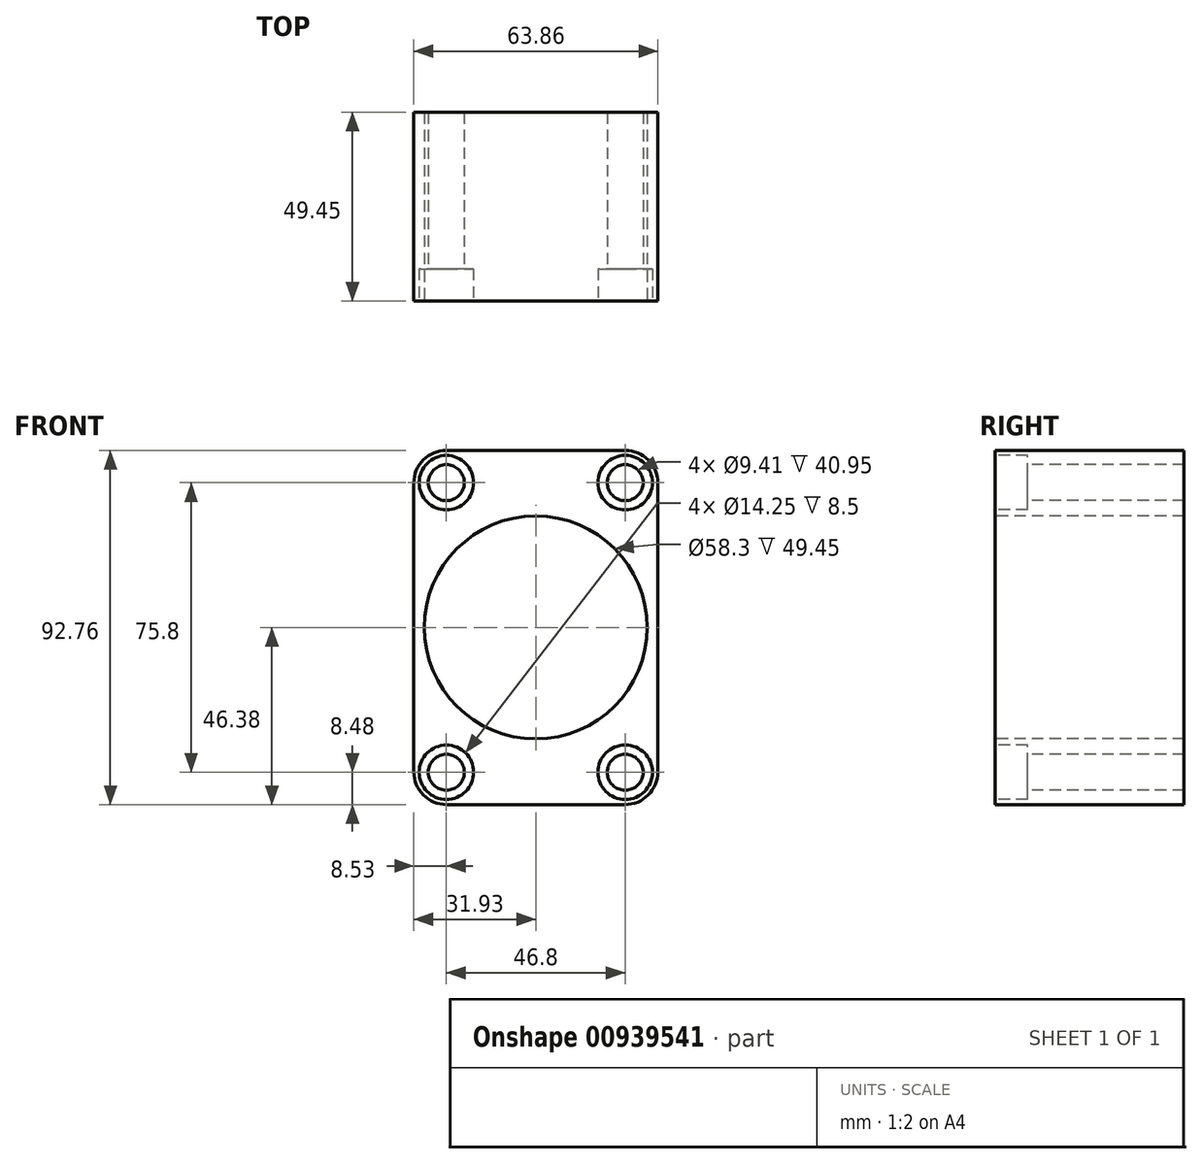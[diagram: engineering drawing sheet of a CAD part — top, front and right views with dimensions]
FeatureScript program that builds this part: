
annotation { "Feature Type Name" : "Feature", "Feature Type Description" : "" }
export const myFeature = defineFeature(function(context is Context, id is Id, definition is map)
    precondition{}
    {
        {
            var Q0;
            Q0=qCreatedBy(makeId("Front.planeOp"),FACE);
            var sketch = newSketch(context, id + "F0", { "sketchPlane" : qUnion([Q0])});
            skLineSegment(sketch, "E0.bottom", {"start": v(-31.93, -46.38) * mm, "end": v(31.93, -46.38) * mm});
            skLineSegment(sketch, "E0.top", {"start": v(-31.93, 46.38) * mm, "end": v(31.93, 46.38) * mm});
            skLineSegment(sketch, "E0.left", {"start": v(-31.93, -46.38) * mm, "end": v(-31.93, 46.38) * mm});
            skLineSegment(sketch, "E0.right", {"start": v(31.93, -46.38) * mm, "end": v(31.93, 46.38) * mm});
            skPoint(sketch, "E0.middle", {"position": v(0, 0) * mm});
            skSolve(sketch);
        }
        {
            var Q0;
            Q0 = qSketchRegion(id + "F0", true);
            extrude(context, id + "F1", {"entities" : qUnion([Q0]), "depth" : 49.45 * mm, "offsetDistance" : 25 * mm});
        }
        {
            var Q0;
            Q0=makeQuery(id+"F1.opExtrude","SWEPT_EDGE",EDGE,{"disambiguationData":[OSD([sQuery(id+"F0.wireOp",EDGE,"E0.top"),sQuery(id+"F0.wireOp",EDGE,"E0.right")])]});
            var Q1;
            Q1=makeQuery(id+"F1.opExtrude","SWEPT_EDGE",EDGE,{"disambiguationData":[OSD([sQuery(id+"F0.wireOp",EDGE,"E0.top"),sQuery(id+"F0.wireOp",EDGE,"E0.left")])]});
            var Q2;
            Q2=makeQuery(id+"F1.opExtrude","SWEPT_EDGE",EDGE,{"disambiguationData":[OSD([sQuery(id+"F0.wireOp",EDGE,"E0.bottom"),sQuery(id+"F0.wireOp",EDGE,"E0.left")])]});
            var Q3;
            Q3=makeQuery(id+"F1.opExtrude","SWEPT_EDGE",EDGE,{"disambiguationData":[OSD([sQuery(id+"F0.wireOp",EDGE,"E0.bottom"),sQuery(id+"F0.wireOp",EDGE,"E0.right")])]});
            fillet(context, id + "F2", {"entities" : qUnion([Q0, Q1, Q2, Q3]), "radius" : 8.6 * mm, "tangentPropagation" : true, "allowEdgeOverflow" : false});
        }
        {
            var Q0;
            Q0=makeQuery(id+"F1.opExtrude","CAP_FACE",FACE,{"disambiguationData":[OSD([sQuery(id+"F0.wireOp",EDGE,"E0.bottom"),sQuery(id+"F0.wireOp",EDGE,"E0.top"),sQuery(id+"F0.wireOp",EDGE,"E0.left"),sQuery(id+"F0.wireOp",EDGE,"E0.right")])],"isStart":false});
            var sketch = newSketch(context, id + "F3", { "sketchPlane" : qUnion([Q0])});
            skCircle(sketch, "E1", {"center": v(-23.4, 37.9) * mm, "radius": 4.7 * mm});
            skCircle(sketch, "E2.MirrorC", {"center": v(23.4, 37.9) * mm, "radius": 4.7 * mm});
            skCircle(sketch, "E3.MirrorC", {"center": v(-23.4, -37.9) * mm, "radius": 4.7 * mm});
            skCircle(sketch, "E4.MirrorC", {"center": v(23.4, -37.9) * mm, "radius": 4.7 * mm});
            skSolve(sketch);
        }
        {
            var Q0;
            Q0 = qSketchRegion(id + "F3", true);
            extrude(context, id + "F4", {"entities" : qUnion([Q0]), "operationType" : NewBodyOperationType.REMOVE, "oppositeDirection" : true, "depth" : 54.1 * mm, "offsetDistance" : 25 * mm});
        }
        {
            var Q0;
            Q0=makeQuery(id+"F1.opExtrude","CAP_FACE",FACE,{"disambiguationData":[OSD([sQuery(id+"F0.wireOp",EDGE,"E0.bottom"),sQuery(id+"F0.wireOp",EDGE,"E0.top"),sQuery(id+"F0.wireOp",EDGE,"E0.left"),sQuery(id+"F0.wireOp",EDGE,"E0.right")])],"isStart":false});
            var sketch = newSketch(context, id + "F5", { "sketchPlane" : qUnion([Q0])});
            skCircle(sketch, "E5", {"center": v(-23.4, 37.9) * mm, "radius": 7.12 * mm});
            skCircle(sketch, "E6.MirrorC", {"center": v(23.4, 37.9) * mm, "radius": 7.12 * mm});
            skCircle(sketch, "E7.MirrorC", {"center": v(-23.4, -37.9) * mm, "radius": 7.12 * mm});
            skCircle(sketch, "E8.MirrorC", {"center": v(23.4, -37.9) * mm, "radius": 7.12 * mm});
            skSolve(sketch);
        }
        {
            var Q0;
            Q0 = qSketchRegion(id + "F5", true);
            extrude(context, id + "F6", {"entities" : qUnion([Q0]), "operationType" : NewBodyOperationType.REMOVE, "oppositeDirection" : true, "depth" : 8.5 * mm, "offsetDistance" : 25 * mm});
        }
        {
            var Q0;
            Q0=makeQuery(id+"F1.opExtrude","CAP_FACE",FACE,{"disambiguationData":[OSD([sQuery(id+"F0.wireOp",EDGE,"E0.bottom"),sQuery(id+"F0.wireOp",EDGE,"E0.top"),sQuery(id+"F0.wireOp",EDGE,"E0.left"),sQuery(id+"F0.wireOp",EDGE,"E0.right")])],"isStart":false});
            var sketch = newSketch(context, id + "F7", { "sketchPlane" : qUnion([Q0])});
            skCircle(sketch, "E9", {"center": v(0, 0) * mm, "radius": 29.15 * mm});
            skSolve(sketch);
        }
        {
            var Q0;
            Q0 = qSketchRegion(id + "F7", true);
            extrude(context, id + "F8", {"entities" : qUnion([Q0]), "operationType" : NewBodyOperationType.REMOVE, "oppositeDirection" : true, "depth" : 69.1 * mm, "offsetDistance" : 25 * mm});
        }
    });
